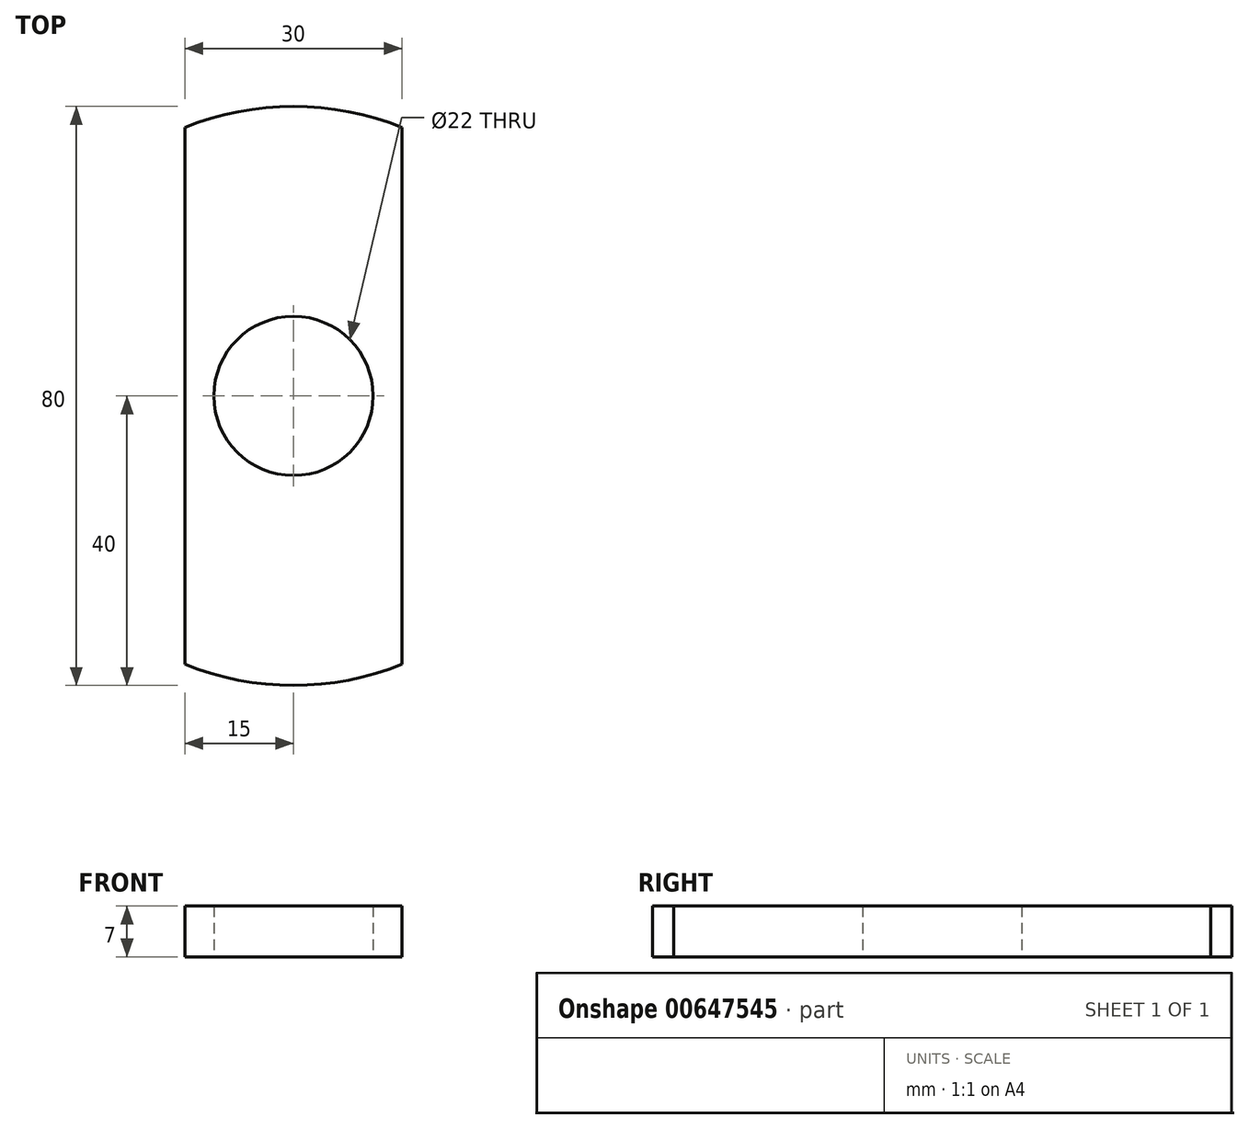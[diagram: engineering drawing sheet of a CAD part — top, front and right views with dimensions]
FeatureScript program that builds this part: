
annotation { "Feature Type Name" : "Feature", "Feature Type Description" : "" }
export const myFeature = defineFeature(function(context is Context, id is Id, definition is map)
    precondition{}
    {
        {
            var Q0;
            Q0=qCreatedBy(makeId("Top.planeOp"),FACE);
            var sketch = newSketch(context, id + "F0", { "sketchPlane" : qUnion([Q0])});
            skArc(sketch, "E0", {"start": v(-15, -37.08) * mm, "mid": v(0, -40) * mm, "end": v(15, -37.08) * mm});
            skLineSegment(sketch, "E1.left", {"start": v(-15, 37.08) * mm, "end": v(-15, -37.08) * mm});
            skLineSegment(sketch, "E1.right", {"start": v(15, 37.08) * mm, "end": v(15, -37.08) * mm});
            skLineSegment(sketch, "E2", {"start": v(-15, 0) * mm, "end": v(0, 0) * mm, "construction": true});
            skLineSegment(sketch, "E3", {"start": v(15, 0) * mm, "end": v(0, 0) * mm, "construction": true});
            skArc(sketch, "E4.trimOffspring", {"start": v(15, 37.08) * mm, "mid": v(0, 40) * mm, "end": v(-15, 37.08) * mm});
            skCircle(sketch, "E5", {"center": v(0, 0) * mm, "radius": 11 * mm});
            skSolve(sketch);
        }
        {
            var Q0;
            Q0=makeQuery(id+"F0.imprint","IMPRINT",FACE,{"disambiguationData":[TD([[makeQuery(id+"F0.imprint","IMPRINT",EDGE,{"derivedFrom":sQuery(id+"F0.wireOp",EDGE,"E0")}),1.0]])]});
            extrude(context, id + "F1", {"entities" : qUnion([Q0]), "depth" : 7 * mm, "offsetDistance" : 25 * mm});
        }
    });
